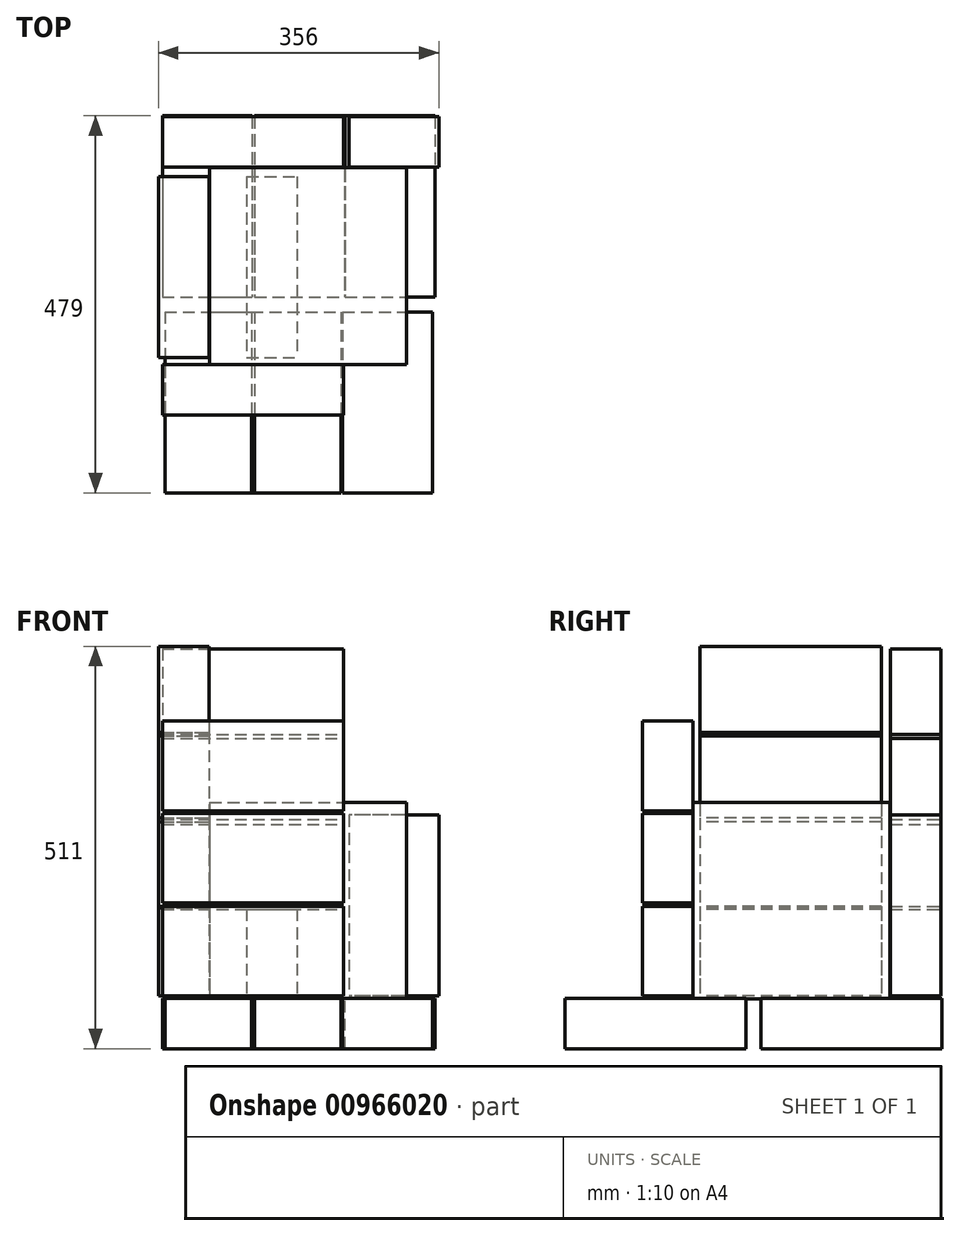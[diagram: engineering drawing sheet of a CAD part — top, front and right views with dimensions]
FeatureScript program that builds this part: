
annotation { "Feature Type Name" : "Feature", "Feature Type Description" : "" }
export const myFeature = defineFeature(function(context is Context, id is Id, definition is map)
    precondition{}
    {
        {
            var Q0;
            Q0=qCreatedBy(makeId("Front.planeOp"),FACE);
            var sketch = newSketch(context, id + "F0", { "sketchPlane" : qUnion([Q0])});
            skLineSegment(sketch, "E0.bottom", {"start": v(0, 114) * mm, "end": v(230, 114) * mm});
            skLineSegment(sketch, "E0.top", {"start": v(0, 0) * mm, "end": v(230, 0) * mm});
            skLineSegment(sketch, "E0.left", {"start": v(0, 114) * mm, "end": v(0, 0) * mm});
            skLineSegment(sketch, "E0.right", {"start": v(230, 114) * mm, "end": v(230, 0) * mm});
            skSolve(sketch);
        }
        {
            var Q0;
            Q0 = qSketchRegion(id + "F0", true);
            extrude(context, id + "F1", {"entities" : qUnion([Q0]), "depth" : 64 * mm, "offsetDistance" : 25 * mm});
        }
        {
            var Q0;
            Q0=qCreatedBy(makeId("Top.planeOp"),FACE);
            var sketch = newSketch(context, id + "F2", { "sketchPlane" : qUnion([Q0])});
            skLineSegment(sketch, "E1.bottom", {"start": v(0, 0) * mm, "end": v(250, 0) * mm});
            skLineSegment(sketch, "E1.top", {"start": v(0, 250) * mm, "end": v(250, 250) * mm});
            skLineSegment(sketch, "E1.left", {"start": v(0, 0) * mm, "end": v(0, 250) * mm});
            skLineSegment(sketch, "E1.right", {"start": v(250, 0) * mm, "end": v(250, 250) * mm});
            skSolve(sketch);
        }
        {
            var Q0;
            Q0 = qSketchRegion(id + "F2", true);
            extrude(context, id + "F3", {"entities" : qUnion([Q0]), "depth" : 250 * mm, "offsetDistance" : 25 * mm});
        }
        {
            var Q0;
            Q0=makeQuery(id+"F1.opExtrude","SWEPT_BODY",BODY,{"disambiguationData":[OSD([sQuery(id+"F0.wireOp",EDGE,"E0.bottom"),sQuery(id+"F0.wireOp",EDGE,"E0.top"),sQuery(id+"F0.wireOp",EDGE,"E0.left"),sQuery(id+"F0.wireOp",EDGE,"E0.right")])]});
            transform(context, id + "F4", {"entities" : qUnion([Q0]), "transformType" : TransformType.TRANSLATION_3D, "dx" : -60 * mm, "dy" : 0 * mm, "dz" : 110 * mm, "makeCopy" : true});
        }
        {
            var Q0;
            Q0=makeQuery(id+"F1.opExtrude","SWEPT_BODY",BODY,{"disambiguationData":[OSD([sQuery(id+"F0.wireOp",EDGE,"E0.bottom"),sQuery(id+"F0.wireOp",EDGE,"E0.top"),sQuery(id+"F0.wireOp",EDGE,"E0.left"),sQuery(id+"F0.wireOp",EDGE,"E0.right")])]});
            transform(context, id + "F5", {"entities" : qUnion([Q0]), "transformType" : TransformType.TRANSLATION_3D, "dx" : -60 * mm, "dy" : 0 * mm, "dz" : 0 * mm, "makeCopy" : false});
        }
        {
            var Q0;
            Q0=makeQuery(id+"F4.opPattern","COPY",BODY,{"derivedFrom":makeQuery(id+"F1.opExtrude","SWEPT_BODY",BODY,{"disambiguationData":[OSD([sQuery(id+"F0.wireOp",EDGE,"E0.bottom"),sQuery(id+"F0.wireOp",EDGE,"E0.top"),sQuery(id+"F0.wireOp",EDGE,"E0.left"),sQuery(id+"F0.wireOp",EDGE,"E0.right")])]}),"instanceName":"1"});
            transform(context, id + "F6", {"entities" : qUnion([Q0]), "transformType" : TransformType.TRANSLATION_3D, "dx" : 0 * mm, "dy" : 315 * mm, "dz" : 0 * mm, "makeCopy" : true});
        }
        {
            var Q0;
            Q0=makeQuery(id+"F1.opExtrude","SWEPT_BODY",BODY,{"disambiguationData":[OSD([sQuery(id+"F0.wireOp",EDGE,"E0.bottom"),sQuery(id+"F0.wireOp",EDGE,"E0.top"),sQuery(id+"F0.wireOp",EDGE,"E0.left"),sQuery(id+"F0.wireOp",EDGE,"E0.right")])]});
            transform(context, id + "F7", {"entities" : qUnion([Q0]), "transformType" : TransformType.TRANSLATION_3D, "dx" : 0 * mm, "dy" : 315 * mm, "dz" : 0 * mm, "makeCopy" : true});
        }
        {
            var Q0;
            Q0=makeQuery(id+"F1.opExtrude","SWEPT_BODY",BODY,{"disambiguationData":[OSD([sQuery(id+"F0.wireOp",EDGE,"E0.bottom"),sQuery(id+"F0.wireOp",EDGE,"E0.top"),sQuery(id+"F0.wireOp",EDGE,"E0.left"),sQuery(id+"F0.wireOp",EDGE,"E0.right")])]});
            transform(context, id + "F8", {"entities" : qUnion([Q0]), "transformType" : TransformType.TRANSLATION_3D, "dx" : -284 * mm, "dy" : 0 * mm, "dz" : 0 * mm, "makeCopy" : true});
        }
        {
            var Q0;
            Q0=makeQuery(id+"F8.opPattern","COPY",BODY,{"derivedFrom":makeQuery(id+"F1.opExtrude","SWEPT_BODY",BODY,{"disambiguationData":[OSD([sQuery(id+"F0.wireOp",EDGE,"E0.bottom"),sQuery(id+"F0.wireOp",EDGE,"E0.top"),sQuery(id+"F0.wireOp",EDGE,"E0.left"),sQuery(id+"F0.wireOp",EDGE,"E0.right")])]}),"instanceName":"1"});
            var Q1;
            Q1=makeQuery(id+"F8.opPattern","COPY",EDGE,{"derivedFrom":makeQuery(id+"F1.opExtrude","CAP_EDGE",EDGE,{"disambiguationData":[OSD([sQuery(id+"F0.wireOp",EDGE,"E0.left")])],"isStart":true}),"instanceName":"1"});
            transform(context, id + "F9", {"entities" : qUnion([Q0]), "transformType" : TransformType.ROTATION, "transformAxis" : qUnion([Q1]), "angle" : 90 * degree, "makeCopy" : false});
        }
        {
            var Q0;
            Q0=makeQuery(id+"F8.opPattern","COPY",BODY,{"derivedFrom":makeQuery(id+"F1.opExtrude","SWEPT_BODY",BODY,{"disambiguationData":[OSD([sQuery(id+"F0.wireOp",EDGE,"E0.bottom"),sQuery(id+"F0.wireOp",EDGE,"E0.top"),sQuery(id+"F0.wireOp",EDGE,"E0.left"),sQuery(id+"F0.wireOp",EDGE,"E0.right")])]}),"instanceName":"1"});
            transform(context, id + "F10", {"entities" : qUnion([Q0]), "transformType" : TransformType.TRANSLATION_3D, "dx" : 343 * mm, "dy" : 239 * mm, "dz" : 0 * mm, "makeCopy" : false});
        }
        {
            var Q0;
            Q0=makeQuery(id+"F1.opExtrude","SWEPT_BODY",BODY,{"disambiguationData":[OSD([sQuery(id+"F0.wireOp",EDGE,"E0.bottom"),sQuery(id+"F0.wireOp",EDGE,"E0.top"),sQuery(id+"F0.wireOp",EDGE,"E0.left"),sQuery(id+"F0.wireOp",EDGE,"E0.right")])]});
            transform(context, id + "F11", {"entities" : qUnion([Q0]), "transformType" : TransformType.TRANSLATION_3D, "dx" : 0 * mm, "dy" : 0 * mm, "dz" : -113 * mm, "makeCopy" : true});
        }
        {
            var Q0;
            Q0=makeQuery(id+"F11.opPattern","COPY",BODY,{"derivedFrom":makeQuery(id+"F1.opExtrude","SWEPT_BODY",BODY,{"disambiguationData":[OSD([sQuery(id+"F0.wireOp",EDGE,"E0.bottom"),sQuery(id+"F0.wireOp",EDGE,"E0.top"),sQuery(id+"F0.wireOp",EDGE,"E0.left"),sQuery(id+"F0.wireOp",EDGE,"E0.right")])]}),"instanceName":"1"});
            var Q1;
            Q1=makeQuery(id+"F11.opPattern","COPY",EDGE,{"derivedFrom":makeQuery(id+"F1.opExtrude","CAP_EDGE",EDGE,{"disambiguationData":[OSD([sQuery(id+"F0.wireOp",EDGE,"E0.bottom")])],"isStart":true}),"instanceName":"1"});
            transform(context, id + "F12", {"entities" : qUnion([Q0]), "transformType" : TransformType.ROTATION, "transformAxis" : qUnion([Q1]), "angle" : 90 * degree, "makeCopy" : false});
        }
        {
            var Q0;
            Q0=makeQuery(id+"F11.opPattern","COPY",BODY,{"derivedFrom":makeQuery(id+"F1.opExtrude","SWEPT_BODY",BODY,{"disambiguationData":[OSD([sQuery(id+"F0.wireOp",EDGE,"E0.bottom"),sQuery(id+"F0.wireOp",EDGE,"E0.top"),sQuery(id+"F0.wireOp",EDGE,"E0.left"),sQuery(id+"F0.wireOp",EDGE,"E0.right")])]}),"instanceName":"1"});
            transform(context, id + "F13", {"entities" : qUnion([Q0]), "transformType" : TransformType.TRANSLATION_3D, "dx" : 0 * mm, "dy" : 212 * mm, "dz" : 0 * mm, "makeCopy" : true});
        }
        {
            var Q0;
            Q0=makeQuery(id+"F11.opPattern","COPY",BODY,{"derivedFrom":makeQuery(id+"F1.opExtrude","SWEPT_BODY",BODY,{"disambiguationData":[OSD([sQuery(id+"F0.wireOp",EDGE,"E0.bottom"),sQuery(id+"F0.wireOp",EDGE,"E0.top"),sQuery(id+"F0.wireOp",EDGE,"E0.left"),sQuery(id+"F0.wireOp",EDGE,"E0.right")])]}),"instanceName":"1"});
            transform(context, id + "F14", {"entities" : qUnion([Q0]), "transformType" : TransformType.TRANSLATION_3D, "dx" : 0 * mm, "dy" : -5 * mm, "dz" : 0 * mm, "makeCopy" : false});
        }
        {
            var Q0;
            Q0=makeQuery(id+"F13.opPattern","COPY",BODY,{"derivedFrom":makeQuery(id+"F11.opPattern","COPY",BODY,{"derivedFrom":makeQuery(id+"F1.opExtrude","SWEPT_BODY",BODY,{"disambiguationData":[OSD([sQuery(id+"F0.wireOp",EDGE,"E0.bottom"),sQuery(id+"F0.wireOp",EDGE,"E0.top"),sQuery(id+"F0.wireOp",EDGE,"E0.left"),sQuery(id+"F0.wireOp",EDGE,"E0.right")])]}),"instanceName":"1"}),"instanceName":"1"});
            transform(context, id + "F15", {"entities" : qUnion([Q0]), "transformType" : TransformType.TRANSLATION_3D, "dx" : 0 * mm, "dy" : 131 * mm, "dz" : 0 * mm, "makeCopy" : true});
        }
        {
            var Q0;
            Q0=makeQuery(id+"F15.opPattern","COPY",BODY,{"derivedFrom":makeQuery(id+"F13.opPattern","COPY",BODY,{"derivedFrom":makeQuery(id+"F11.opPattern","COPY",BODY,{"derivedFrom":makeQuery(id+"F1.opExtrude","SWEPT_BODY",BODY,{"disambiguationData":[OSD([sQuery(id+"F0.wireOp",EDGE,"E0.bottom"),sQuery(id+"F0.wireOp",EDGE,"E0.top"),sQuery(id+"F0.wireOp",EDGE,"E0.left"),sQuery(id+"F0.wireOp",EDGE,"E0.right")])]}),"instanceName":"1"}),"instanceName":"1"}),"instanceName":"1"});
            var Q1;
            Q1=makeQuery(id+"F15.opPattern","COPY",EDGE,{"derivedFrom":makeQuery(id+"F13.opPattern","COPY",EDGE,{"derivedFrom":makeQuery(id+"F11.opPattern","COPY",EDGE,{"derivedFrom":makeQuery(id+"F1.opExtrude","SWEPT_EDGE",EDGE,{"disambiguationData":[OSD([sQuery(id+"F0.wireOp",EDGE,"E0.bottom"),sQuery(id+"F0.wireOp",EDGE,"E0.left")])]}),"instanceName":"1"}),"instanceName":"1"}),"instanceName":"1"});
            transform(context, id + "F16", {"entities" : qUnion([Q0]), "transformType" : TransformType.ROTATION, "transformAxis" : qUnion([Q1]), "angle" : 90 * degree, "oppositeDirection" : true, "makeCopy" : false});
        }
        {
            var Q0;
            Q0=makeQuery(id+"F15.opPattern","COPY",BODY,{"derivedFrom":makeQuery(id+"F13.opPattern","COPY",BODY,{"derivedFrom":makeQuery(id+"F11.opPattern","COPY",BODY,{"derivedFrom":makeQuery(id+"F1.opExtrude","SWEPT_BODY",BODY,{"disambiguationData":[OSD([sQuery(id+"F0.wireOp",EDGE,"E0.bottom"),sQuery(id+"F0.wireOp",EDGE,"E0.top"),sQuery(id+"F0.wireOp",EDGE,"E0.left"),sQuery(id+"F0.wireOp",EDGE,"E0.right")])]}),"instanceName":"1"}),"instanceName":"1"}),"instanceName":"1"});
            transform(context, id + "F17", {"entities" : qUnion([Q0]), "transformType" : TransformType.TRANSLATION_3D, "dx" : 0 * mm, "dy" : -27 * mm, "dz" : 0 * mm, "makeCopy" : false});
        }
        {
            var Q0;
            Q0=makeQuery(id+"F13.opPattern","COPY",BODY,{"derivedFrom":makeQuery(id+"F11.opPattern","COPY",BODY,{"derivedFrom":makeQuery(id+"F1.opExtrude","SWEPT_BODY",BODY,{"disambiguationData":[OSD([sQuery(id+"F0.wireOp",EDGE,"E0.bottom"),sQuery(id+"F0.wireOp",EDGE,"E0.top"),sQuery(id+"F0.wireOp",EDGE,"E0.left"),sQuery(id+"F0.wireOp",EDGE,"E0.right")])]}),"instanceName":"1"}),"instanceName":"1"});
            deleteBodies(context, id + "F18", {"entities" : qUnion([Q0])});
        }
        {
            var Q0;
            Q0=makeQuery(id+"F11.opPattern","COPY",BODY,{"derivedFrom":makeQuery(id+"F1.opExtrude","SWEPT_BODY",BODY,{"disambiguationData":[OSD([sQuery(id+"F0.wireOp",EDGE,"E0.bottom"),sQuery(id+"F0.wireOp",EDGE,"E0.top"),sQuery(id+"F0.wireOp",EDGE,"E0.left"),sQuery(id+"F0.wireOp",EDGE,"E0.right")])]}),"instanceName":"1"});
            deleteBodies(context, id + "F19", {"entities" : qUnion([Q0])});
        }
        {
            var Q0;
            Q0=makeQuery(id+"F15.opPattern","COPY",BODY,{"derivedFrom":makeQuery(id+"F13.opPattern","COPY",BODY,{"derivedFrom":makeQuery(id+"F11.opPattern","COPY",BODY,{"derivedFrom":makeQuery(id+"F1.opExtrude","SWEPT_BODY",BODY,{"disambiguationData":[OSD([sQuery(id+"F0.wireOp",EDGE,"E0.bottom"),sQuery(id+"F0.wireOp",EDGE,"E0.top"),sQuery(id+"F0.wireOp",EDGE,"E0.left"),sQuery(id+"F0.wireOp",EDGE,"E0.right")])]}),"instanceName":"1"}),"instanceName":"1"}),"instanceName":"1"});
            transform(context, id + "F20", {"entities" : qUnion([Q0]), "transformType" : TransformType.TRANSLATION_3D, "dx" : 0 * mm, "dy" : -236 * mm, "dz" : 0 * mm, "makeCopy" : true});
        }
        {
            var Q0;
            Q0=makeQuery(id+"F20.opPattern","COPY",BODY,{"derivedFrom":makeQuery(id+"F15.opPattern","COPY",BODY,{"derivedFrom":makeQuery(id+"F13.opPattern","COPY",BODY,{"derivedFrom":makeQuery(id+"F11.opPattern","COPY",BODY,{"derivedFrom":makeQuery(id+"F1.opExtrude","SWEPT_BODY",BODY,{"disambiguationData":[OSD([sQuery(id+"F0.wireOp",EDGE,"E0.bottom"),sQuery(id+"F0.wireOp",EDGE,"E0.top"),sQuery(id+"F0.wireOp",EDGE,"E0.left"),sQuery(id+"F0.wireOp",EDGE,"E0.right")])]}),"instanceName":"1"}),"instanceName":"1"}),"instanceName":"1"}),"instanceName":"1"});
            var Q1;
            Q1=makeQuery(id+"F20.opPattern","COPY",EDGE,{"derivedFrom":makeQuery(id+"F15.opPattern","COPY",EDGE,{"derivedFrom":makeQuery(id+"F13.opPattern","COPY",EDGE,{"derivedFrom":makeQuery(id+"F11.opPattern","COPY",EDGE,{"derivedFrom":makeQuery(id+"F1.opExtrude","SWEPT_EDGE",EDGE,{"disambiguationData":[OSD([sQuery(id+"F0.wireOp",EDGE,"E0.top"),sQuery(id+"F0.wireOp",EDGE,"E0.left")])]}),"instanceName":"1"}),"instanceName":"1"}),"instanceName":"1"}),"instanceName":"1"});
            transform(context, id + "F21", {"entities" : qUnion([Q0]), "transformType" : TransformType.ROTATION, "transformAxis" : qUnion([Q1]), "angle" : 90 * degree, "makeCopy" : false});
        }
        {
            var Q0;
            Q0=makeQuery(id+"F15.opPattern","COPY",BODY,{"derivedFrom":makeQuery(id+"F13.opPattern","COPY",BODY,{"derivedFrom":makeQuery(id+"F11.opPattern","COPY",BODY,{"derivedFrom":makeQuery(id+"F1.opExtrude","SWEPT_BODY",BODY,{"disambiguationData":[OSD([sQuery(id+"F0.wireOp",EDGE,"E0.bottom"),sQuery(id+"F0.wireOp",EDGE,"E0.top"),sQuery(id+"F0.wireOp",EDGE,"E0.left"),sQuery(id+"F0.wireOp",EDGE,"E0.right")])]}),"instanceName":"1"}),"instanceName":"1"}),"instanceName":"1"});
            transform(context, id + "F22", {"entities" : qUnion([Q0]), "transformType" : TransformType.TRANSLATION_3D, "dx" : 108 * mm, "dy" : 0 * mm, "dz" : 0 * mm, "makeCopy" : true});
        }
        {
            var Q0;
            Q0=makeQuery(id+"F20.opPattern","COPY",BODY,{"derivedFrom":makeQuery(id+"F15.opPattern","COPY",BODY,{"derivedFrom":makeQuery(id+"F13.opPattern","COPY",BODY,{"derivedFrom":makeQuery(id+"F11.opPattern","COPY",BODY,{"derivedFrom":makeQuery(id+"F1.opExtrude","SWEPT_BODY",BODY,{"disambiguationData":[OSD([sQuery(id+"F0.wireOp",EDGE,"E0.bottom"),sQuery(id+"F0.wireOp",EDGE,"E0.top"),sQuery(id+"F0.wireOp",EDGE,"E0.left"),sQuery(id+"F0.wireOp",EDGE,"E0.right")])]}),"instanceName":"1"}),"instanceName":"1"}),"instanceName":"1"}),"instanceName":"1"});
            var Q1;
            Q1=makeQuery(id+"F20.opPattern","COPY",EDGE,{"derivedFrom":makeQuery(id+"F15.opPattern","COPY",EDGE,{"derivedFrom":makeQuery(id+"F13.opPattern","COPY",EDGE,{"derivedFrom":makeQuery(id+"F11.opPattern","COPY",EDGE,{"derivedFrom":makeQuery(id+"F1.opExtrude","SWEPT_EDGE",EDGE,{"disambiguationData":[OSD([sQuery(id+"F0.wireOp",EDGE,"E0.bottom"),sQuery(id+"F0.wireOp",EDGE,"E0.left")])]}),"instanceName":"1"}),"instanceName":"1"}),"instanceName":"1"}),"instanceName":"1"});
            transform(context, id + "F23", {"entities" : qUnion([Q0]), "transformType" : TransformType.ROTATION, "transformAxis" : qUnion([Q1]), "angle" : 90 * degree, "oppositeDirection" : true, "makeCopy" : true});
        }
        {
            var Q0;
            Q0=makeQuery(id+"F23.opPattern","COPY",BODY,{"derivedFrom":makeQuery(id+"F20.opPattern","COPY",BODY,{"derivedFrom":makeQuery(id+"F15.opPattern","COPY",BODY,{"derivedFrom":makeQuery(id+"F13.opPattern","COPY",BODY,{"derivedFrom":makeQuery(id+"F11.opPattern","COPY",BODY,{"derivedFrom":makeQuery(id+"F1.opExtrude","SWEPT_BODY",BODY,{"disambiguationData":[OSD([sQuery(id+"F0.wireOp",EDGE,"E0.bottom"),sQuery(id+"F0.wireOp",EDGE,"E0.top"),sQuery(id+"F0.wireOp",EDGE,"E0.left"),sQuery(id+"F0.wireOp",EDGE,"E0.right")])]}),"instanceName":"1"}),"instanceName":"1"}),"instanceName":"1"}),"instanceName":"1"}),"instanceName":"1"});
            transform(context, id + "F24", {"entities" : qUnion([Q0]), "transformType" : TransformType.TRANSLATION_3D, "dx" : -111 * mm, "dy" : 101 * mm, "dz" : 0 * mm, "makeCopy" : false});
        }
        {
            var Q0;
            Q0=makeQuery(id+"F20.opPattern","COPY",BODY,{"derivedFrom":makeQuery(id+"F15.opPattern","COPY",BODY,{"derivedFrom":makeQuery(id+"F13.opPattern","COPY",BODY,{"derivedFrom":makeQuery(id+"F11.opPattern","COPY",BODY,{"derivedFrom":makeQuery(id+"F1.opExtrude","SWEPT_BODY",BODY,{"disambiguationData":[OSD([sQuery(id+"F0.wireOp",EDGE,"E0.bottom"),sQuery(id+"F0.wireOp",EDGE,"E0.top"),sQuery(id+"F0.wireOp",EDGE,"E0.left"),sQuery(id+"F0.wireOp",EDGE,"E0.right")])]}),"instanceName":"1"}),"instanceName":"1"}),"instanceName":"1"}),"instanceName":"1"});
            deleteBodies(context, id + "F25", {"entities" : qUnion([Q0])});
        }
        {
            var Q0;
            Q0=makeQuery(id+"F23.opPattern","COPY",BODY,{"derivedFrom":makeQuery(id+"F20.opPattern","COPY",BODY,{"derivedFrom":makeQuery(id+"F15.opPattern","COPY",BODY,{"derivedFrom":makeQuery(id+"F13.opPattern","COPY",BODY,{"derivedFrom":makeQuery(id+"F11.opPattern","COPY",BODY,{"derivedFrom":makeQuery(id+"F1.opExtrude","SWEPT_BODY",BODY,{"disambiguationData":[OSD([sQuery(id+"F0.wireOp",EDGE,"E0.bottom"),sQuery(id+"F0.wireOp",EDGE,"E0.top"),sQuery(id+"F0.wireOp",EDGE,"E0.left"),sQuery(id+"F0.wireOp",EDGE,"E0.right")])]}),"instanceName":"1"}),"instanceName":"1"}),"instanceName":"1"}),"instanceName":"1"}),"instanceName":"1"});
            transform(context, id + "F26", {"entities" : qUnion([Q0]), "transformType" : TransformType.TRANSLATION_3D, "dx" : 110 * mm, "dy" : 0 * mm, "dz" : 0 * mm, "makeCopy" : true});
        }
        {
            var Q0;
            Q0=makeQuery(id+"F22.opPattern","COPY",BODY,{"derivedFrom":makeQuery(id+"F15.opPattern","COPY",BODY,{"derivedFrom":makeQuery(id+"F13.opPattern","COPY",BODY,{"derivedFrom":makeQuery(id+"F11.opPattern","COPY",BODY,{"derivedFrom":makeQuery(id+"F1.opExtrude","SWEPT_BODY",BODY,{"disambiguationData":[OSD([sQuery(id+"F0.wireOp",EDGE,"E0.bottom"),sQuery(id+"F0.wireOp",EDGE,"E0.top"),sQuery(id+"F0.wireOp",EDGE,"E0.left"),sQuery(id+"F0.wireOp",EDGE,"E0.right")])]}),"instanceName":"1"}),"instanceName":"1"}),"instanceName":"1"}),"instanceName":"1"});
            transform(context, id + "F27", {"entities" : qUnion([Q0]), "transformType" : TransformType.TRANSLATION_3D, "dx" : 112 * mm, "dy" : 0 * mm, "dz" : 0 * mm, "makeCopy" : true});
        }
        {
            var Q0;
            Q0=makeQuery(id+"F8.opPattern","COPY",BODY,{"derivedFrom":makeQuery(id+"F1.opExtrude","SWEPT_BODY",BODY,{"disambiguationData":[OSD([sQuery(id+"F0.wireOp",EDGE,"E0.bottom"),sQuery(id+"F0.wireOp",EDGE,"E0.top"),sQuery(id+"F0.wireOp",EDGE,"E0.left"),sQuery(id+"F0.wireOp",EDGE,"E0.right")])]}),"instanceName":"1"});
            transform(context, id + "F28", {"entities" : qUnion([Q0]), "transformType" : TransformType.TRANSLATION_3D, "dx" : 112 * mm, "dy" : 0 * mm, "dz" : 0 * mm, "makeCopy" : true});
        }
        {
            var Q0;
            Q0=makeQuery(id+"F8.opPattern","COPY",BODY,{"derivedFrom":makeQuery(id+"F1.opExtrude","SWEPT_BODY",BODY,{"disambiguationData":[OSD([sQuery(id+"F0.wireOp",EDGE,"E0.bottom"),sQuery(id+"F0.wireOp",EDGE,"E0.top"),sQuery(id+"F0.wireOp",EDGE,"E0.left"),sQuery(id+"F0.wireOp",EDGE,"E0.right")])]}),"instanceName":"1"});
            transform(context, id + "F29", {"entities" : qUnion([Q0]), "transformType" : TransformType.TRANSLATION_3D, "dx" : 0 * mm, "dy" : 0 * mm, "dz" : 112 * mm, "makeCopy" : true});
        }
        {
            var Q0;
            Q0=makeQuery(id+"F6.opPattern","COPY",BODY,{"derivedFrom":makeQuery(id+"F4.opPattern","COPY",BODY,{"derivedFrom":makeQuery(id+"F1.opExtrude","SWEPT_BODY",BODY,{"disambiguationData":[OSD([sQuery(id+"F0.wireOp",EDGE,"E0.bottom"),sQuery(id+"F0.wireOp",EDGE,"E0.top"),sQuery(id+"F0.wireOp",EDGE,"E0.left"),sQuery(id+"F0.wireOp",EDGE,"E0.right")])]}),"instanceName":"1"}),"instanceName":"1"});
            transform(context, id + "F30", {"entities" : qUnion([Q0]), "transformType" : TransformType.TRANSLATION_3D, "dx" : 0 * mm, "dy" : 0 * mm, "dz" : 108 * mm, "makeCopy" : true});
        }
        {
            var Q0;
            Q0=makeQuery(id+"F7.opPattern","COPY",BODY,{"derivedFrom":makeQuery(id+"F1.opExtrude","SWEPT_BODY",BODY,{"disambiguationData":[OSD([sQuery(id+"F0.wireOp",EDGE,"E0.bottom"),sQuery(id+"F0.wireOp",EDGE,"E0.top"),sQuery(id+"F0.wireOp",EDGE,"E0.left"),sQuery(id+"F0.wireOp",EDGE,"E0.right")])]}),"instanceName":"1"});
            transform(context, id + "F31", {"entities" : qUnion([Q0]), "transformType" : TransformType.TRANSLATION_3D, "dx" : 7 * mm, "dy" : 0 * mm, "dz" : 0 * mm, "makeCopy" : true});
        }
        {
            var Q0;
            Q0=makeQuery(id+"F31.opPattern","COPY",BODY,{"derivedFrom":makeQuery(id+"F7.opPattern","COPY",BODY,{"derivedFrom":makeQuery(id+"F1.opExtrude","SWEPT_BODY",BODY,{"disambiguationData":[OSD([sQuery(id+"F0.wireOp",EDGE,"E0.bottom"),sQuery(id+"F0.wireOp",EDGE,"E0.top"),sQuery(id+"F0.wireOp",EDGE,"E0.left"),sQuery(id+"F0.wireOp",EDGE,"E0.right")])]}),"instanceName":"1"}),"instanceName":"1"});
            var Q1;
            Q1=makeQuery(id+"F31.opPattern","COPY",EDGE,{"derivedFrom":makeQuery(id+"F7.opPattern","COPY",EDGE,{"derivedFrom":makeQuery(id+"F1.opExtrude","SWEPT_EDGE",EDGE,{"disambiguationData":[OSD([sQuery(id+"F0.wireOp",EDGE,"E0.top"),sQuery(id+"F0.wireOp",EDGE,"E0.right")])]}),"instanceName":"1"}),"instanceName":"1"});
            transform(context, id + "F32", {"entities" : qUnion([Q0]), "transformType" : TransformType.ROTATION, "transformAxis" : qUnion([Q1]), "angle" : 90 * degree, "makeCopy" : false});
        }
        {
            var Q0;
            Q0=makeQuery(id+"F30.opPattern","COPY",BODY,{"derivedFrom":makeQuery(id+"F6.opPattern","COPY",BODY,{"derivedFrom":makeQuery(id+"F4.opPattern","COPY",BODY,{"derivedFrom":makeQuery(id+"F1.opExtrude","SWEPT_BODY",BODY,{"disambiguationData":[OSD([sQuery(id+"F0.wireOp",EDGE,"E0.bottom"),sQuery(id+"F0.wireOp",EDGE,"E0.top"),sQuery(id+"F0.wireOp",EDGE,"E0.left"),sQuery(id+"F0.wireOp",EDGE,"E0.right")])]}),"instanceName":"1"}),"instanceName":"1"}),"instanceName":"1"});
            var Q1;
            Q1=makeQuery(id+"F29.opPattern","COPY",BODY,{"derivedFrom":makeQuery(id+"F8.opPattern","COPY",BODY,{"derivedFrom":makeQuery(id+"F1.opExtrude","SWEPT_BODY",BODY,{"disambiguationData":[OSD([sQuery(id+"F0.wireOp",EDGE,"E0.bottom"),sQuery(id+"F0.wireOp",EDGE,"E0.top"),sQuery(id+"F0.wireOp",EDGE,"E0.left"),sQuery(id+"F0.wireOp",EDGE,"E0.right")])]}),"instanceName":"1"}),"instanceName":"1"});
            transform(context, id + "F33", {"entities" : qUnion([Q0, Q1]), "transformType" : TransformType.TRANSLATION_3D, "dx" : 0 * mm, "dy" : 0 * mm, "dz" : 109 * mm, "makeCopy" : true});
        }
        {
            var Q0;
            Q0=makeQuery(id+"F33.opPattern","COPY",BODY,{"derivedFrom":makeQuery(id+"F29.opPattern","COPY",BODY,{"derivedFrom":makeQuery(id+"F8.opPattern","COPY",BODY,{"derivedFrom":makeQuery(id+"F1.opExtrude","SWEPT_BODY",BODY,{"disambiguationData":[OSD([sQuery(id+"F0.wireOp",EDGE,"E0.bottom"),sQuery(id+"F0.wireOp",EDGE,"E0.top"),sQuery(id+"F0.wireOp",EDGE,"E0.left"),sQuery(id+"F0.wireOp",EDGE,"E0.right")])]}),"instanceName":"1"}),"instanceName":"1"}),"instanceName":"1"});
            transform(context, id + "F34", {"entities" : qUnion([Q0]), "transformType" : TransformType.TRANSLATION_3D, "dx" : 0 * mm, "dy" : 0 * mm, "dz" : 109 * mm, "makeCopy" : true});
        }
        {
            var Q0;
            Q0=makeQuery(id+"F27.opPattern","COPY",BODY,{"derivedFrom":makeQuery(id+"F22.opPattern","COPY",BODY,{"derivedFrom":makeQuery(id+"F15.opPattern","COPY",BODY,{"derivedFrom":makeQuery(id+"F13.opPattern","COPY",BODY,{"derivedFrom":makeQuery(id+"F11.opPattern","COPY",BODY,{"derivedFrom":makeQuery(id+"F1.opExtrude","SWEPT_BODY",BODY,{"disambiguationData":[OSD([sQuery(id+"F0.wireOp",EDGE,"E0.bottom"),sQuery(id+"F0.wireOp",EDGE,"E0.top"),sQuery(id+"F0.wireOp",EDGE,"E0.left"),sQuery(id+"F0.wireOp",EDGE,"E0.right")])]}),"instanceName":"1"}),"instanceName":"1"}),"instanceName":"1"}),"instanceName":"1"}),"instanceName":"1"});
            transform(context, id + "F35", {"entities" : qUnion([Q0]), "transformType" : TransformType.TRANSLATION_3D, "dx" : 112 * mm, "dy" : 0 * mm, "dz" : 0 * mm, "makeCopy" : true});
        }
        {
            var Q0;
            Q0=makeQuery(id+"F4.opPattern","COPY",BODY,{"derivedFrom":makeQuery(id+"F1.opExtrude","SWEPT_BODY",BODY,{"disambiguationData":[OSD([sQuery(id+"F0.wireOp",EDGE,"E0.bottom"),sQuery(id+"F0.wireOp",EDGE,"E0.top"),sQuery(id+"F0.wireOp",EDGE,"E0.left"),sQuery(id+"F0.wireOp",EDGE,"E0.right")])]}),"instanceName":"1"});
            transform(context, id + "F36", {"entities" : qUnion([Q0]), "transformType" : TransformType.TRANSLATION_3D, "dx" : 0 * mm, "dy" : 0 * mm, "dz" : 8 * mm, "makeCopy" : false});
        }
        {
            var Q0;
            Q0=makeQuery(id+"F35.opPattern","COPY",BODY,{"derivedFrom":makeQuery(id+"F27.opPattern","COPY",BODY,{"derivedFrom":makeQuery(id+"F22.opPattern","COPY",BODY,{"derivedFrom":makeQuery(id+"F15.opPattern","COPY",BODY,{"derivedFrom":makeQuery(id+"F13.opPattern","COPY",BODY,{"derivedFrom":makeQuery(id+"F11.opPattern","COPY",BODY,{"derivedFrom":makeQuery(id+"F1.opExtrude","SWEPT_BODY",BODY,{"disambiguationData":[OSD([sQuery(id+"F0.wireOp",EDGE,"E0.bottom"),sQuery(id+"F0.wireOp",EDGE,"E0.top"),sQuery(id+"F0.wireOp",EDGE,"E0.left"),sQuery(id+"F0.wireOp",EDGE,"E0.right")])]}),"instanceName":"1"}),"instanceName":"1"}),"instanceName":"1"}),"instanceName":"1"}),"instanceName":"1"}),"instanceName":"1"});
            deleteBodies(context, id + "F37", {"entities" : qUnion([Q0])});
        }
        {
            var Q0;
            Q0=makeQuery(id+"F22.opPattern","COPY",BODY,{"derivedFrom":makeQuery(id+"F15.opPattern","COPY",BODY,{"derivedFrom":makeQuery(id+"F13.opPattern","COPY",BODY,{"derivedFrom":makeQuery(id+"F11.opPattern","COPY",BODY,{"derivedFrom":makeQuery(id+"F1.opExtrude","SWEPT_BODY",BODY,{"disambiguationData":[OSD([sQuery(id+"F0.wireOp",EDGE,"E0.bottom"),sQuery(id+"F0.wireOp",EDGE,"E0.top"),sQuery(id+"F0.wireOp",EDGE,"E0.left"),sQuery(id+"F0.wireOp",EDGE,"E0.right")])]}),"instanceName":"1"}),"instanceName":"1"}),"instanceName":"1"}),"instanceName":"1"});
            var Q1;
            Q1=makeQuery(id+"F27.opPattern","COPY",BODY,{"derivedFrom":makeQuery(id+"F22.opPattern","COPY",BODY,{"derivedFrom":makeQuery(id+"F15.opPattern","COPY",BODY,{"derivedFrom":makeQuery(id+"F13.opPattern","COPY",BODY,{"derivedFrom":makeQuery(id+"F11.opPattern","COPY",BODY,{"derivedFrom":makeQuery(id+"F1.opExtrude","SWEPT_BODY",BODY,{"disambiguationData":[OSD([sQuery(id+"F0.wireOp",EDGE,"E0.bottom"),sQuery(id+"F0.wireOp",EDGE,"E0.top"),sQuery(id+"F0.wireOp",EDGE,"E0.left"),sQuery(id+"F0.wireOp",EDGE,"E0.right")])]}),"instanceName":"1"}),"instanceName":"1"}),"instanceName":"1"}),"instanceName":"1"}),"instanceName":"1"});
            transform(context, id + "F38", {"entities" : qUnion([Q0, Q1]), "transformType" : TransformType.TRANSLATION_3D, "dx" : 9 * mm, "dy" : 0 * mm, "dz" : 0 * mm, "makeCopy" : false});
        }
        {
            var Q0;
            Q0=makeQuery(id+"F27.opPattern","COPY",BODY,{"derivedFrom":makeQuery(id+"F22.opPattern","COPY",BODY,{"derivedFrom":makeQuery(id+"F15.opPattern","COPY",BODY,{"derivedFrom":makeQuery(id+"F13.opPattern","COPY",BODY,{"derivedFrom":makeQuery(id+"F11.opPattern","COPY",BODY,{"derivedFrom":makeQuery(id+"F1.opExtrude","SWEPT_BODY",BODY,{"disambiguationData":[OSD([sQuery(id+"F0.wireOp",EDGE,"E0.bottom"),sQuery(id+"F0.wireOp",EDGE,"E0.top"),sQuery(id+"F0.wireOp",EDGE,"E0.left"),sQuery(id+"F0.wireOp",EDGE,"E0.right")])]}),"instanceName":"1"}),"instanceName":"1"}),"instanceName":"1"}),"instanceName":"1"}),"instanceName":"1"});
            transform(context, id + "F39", {"entities" : qUnion([Q0]), "transformType" : TransformType.TRANSLATION_3D, "dx" : 3 * mm, "dy" : 0 * mm, "dz" : 0 * mm, "makeCopy" : false});
        }
        {
            var Q0;
            Q0=makeQuery(id+"F31.opPattern","COPY",BODY,{"derivedFrom":makeQuery(id+"F7.opPattern","COPY",BODY,{"derivedFrom":makeQuery(id+"F1.opExtrude","SWEPT_BODY",BODY,{"disambiguationData":[OSD([sQuery(id+"F0.wireOp",EDGE,"E0.bottom"),sQuery(id+"F0.wireOp",EDGE,"E0.top"),sQuery(id+"F0.wireOp",EDGE,"E0.left"),sQuery(id+"F0.wireOp",EDGE,"E0.right")])]}),"instanceName":"1"}),"instanceName":"1"});
            var Q1;
            Q1=makeQuery(id+"F6.opPattern","COPY",BODY,{"derivedFrom":makeQuery(id+"F4.opPattern","COPY",BODY,{"derivedFrom":makeQuery(id+"F1.opExtrude","SWEPT_BODY",BODY,{"disambiguationData":[OSD([sQuery(id+"F0.wireOp",EDGE,"E0.bottom"),sQuery(id+"F0.wireOp",EDGE,"E0.top"),sQuery(id+"F0.wireOp",EDGE,"E0.left"),sQuery(id+"F0.wireOp",EDGE,"E0.right")])]}),"instanceName":"1"}),"instanceName":"1"});
            var Q2;
            Q2=makeQuery(id+"F30.opPattern","COPY",BODY,{"derivedFrom":makeQuery(id+"F6.opPattern","COPY",BODY,{"derivedFrom":makeQuery(id+"F4.opPattern","COPY",BODY,{"derivedFrom":makeQuery(id+"F1.opExtrude","SWEPT_BODY",BODY,{"disambiguationData":[OSD([sQuery(id+"F0.wireOp",EDGE,"E0.bottom"),sQuery(id+"F0.wireOp",EDGE,"E0.top"),sQuery(id+"F0.wireOp",EDGE,"E0.left"),sQuery(id+"F0.wireOp",EDGE,"E0.right")])]}),"instanceName":"1"}),"instanceName":"1"}),"instanceName":"1"});
            var Q3;
            Q3=makeQuery(id+"F33.opPattern","COPY",BODY,{"derivedFrom":makeQuery(id+"F30.opPattern","COPY",BODY,{"derivedFrom":makeQuery(id+"F6.opPattern","COPY",BODY,{"derivedFrom":makeQuery(id+"F4.opPattern","COPY",BODY,{"derivedFrom":makeQuery(id+"F1.opExtrude","SWEPT_BODY",BODY,{"disambiguationData":[OSD([sQuery(id+"F0.wireOp",EDGE,"E0.bottom"),sQuery(id+"F0.wireOp",EDGE,"E0.top"),sQuery(id+"F0.wireOp",EDGE,"E0.left"),sQuery(id+"F0.wireOp",EDGE,"E0.right")])]}),"instanceName":"1"}),"instanceName":"1"}),"instanceName":"1"}),"instanceName":"1"});
            var Q4;
            Q4=makeQuery(id+"F7.opPattern","COPY",BODY,{"derivedFrom":makeQuery(id+"F1.opExtrude","SWEPT_BODY",BODY,{"disambiguationData":[OSD([sQuery(id+"F0.wireOp",EDGE,"E0.bottom"),sQuery(id+"F0.wireOp",EDGE,"E0.top"),sQuery(id+"F0.wireOp",EDGE,"E0.left"),sQuery(id+"F0.wireOp",EDGE,"E0.right")])]}),"instanceName":"1"});
            var Q5;
            Q5=makeQuery(id+"F8.opPattern","COPY",BODY,{"derivedFrom":makeQuery(id+"F1.opExtrude","SWEPT_BODY",BODY,{"disambiguationData":[OSD([sQuery(id+"F0.wireOp",EDGE,"E0.bottom"),sQuery(id+"F0.wireOp",EDGE,"E0.top"),sQuery(id+"F0.wireOp",EDGE,"E0.left"),sQuery(id+"F0.wireOp",EDGE,"E0.right")])]}),"instanceName":"1"});
            var Q6;
            Q6=makeQuery(id+"F1.opExtrude","SWEPT_BODY",BODY,{"disambiguationData":[OSD([sQuery(id+"F0.wireOp",EDGE,"E0.bottom"),sQuery(id+"F0.wireOp",EDGE,"E0.top"),sQuery(id+"F0.wireOp",EDGE,"E0.left"),sQuery(id+"F0.wireOp",EDGE,"E0.right")])]});
            var Q7;
            Q7=makeQuery(id+"F4.opPattern","COPY",BODY,{"derivedFrom":makeQuery(id+"F1.opExtrude","SWEPT_BODY",BODY,{"disambiguationData":[OSD([sQuery(id+"F0.wireOp",EDGE,"E0.bottom"),sQuery(id+"F0.wireOp",EDGE,"E0.top"),sQuery(id+"F0.wireOp",EDGE,"E0.left"),sQuery(id+"F0.wireOp",EDGE,"E0.right")])]}),"instanceName":"1"});
            var Q8;
            Q8=makeQuery(id+"F29.opPattern","COPY",BODY,{"derivedFrom":makeQuery(id+"F8.opPattern","COPY",BODY,{"derivedFrom":makeQuery(id+"F1.opExtrude","SWEPT_BODY",BODY,{"disambiguationData":[OSD([sQuery(id+"F0.wireOp",EDGE,"E0.bottom"),sQuery(id+"F0.wireOp",EDGE,"E0.top"),sQuery(id+"F0.wireOp",EDGE,"E0.left"),sQuery(id+"F0.wireOp",EDGE,"E0.right")])]}),"instanceName":"1"}),"instanceName":"1"});
            var Q9;
            Q9=makeQuery(id+"F33.opPattern","COPY",BODY,{"derivedFrom":makeQuery(id+"F29.opPattern","COPY",BODY,{"derivedFrom":makeQuery(id+"F8.opPattern","COPY",BODY,{"derivedFrom":makeQuery(id+"F1.opExtrude","SWEPT_BODY",BODY,{"disambiguationData":[OSD([sQuery(id+"F0.wireOp",EDGE,"E0.bottom"),sQuery(id+"F0.wireOp",EDGE,"E0.top"),sQuery(id+"F0.wireOp",EDGE,"E0.left"),sQuery(id+"F0.wireOp",EDGE,"E0.right")])]}),"instanceName":"1"}),"instanceName":"1"}),"instanceName":"1"});
            var Q10;
            Q10=makeQuery(id+"F34.opPattern","COPY",BODY,{"derivedFrom":makeQuery(id+"F33.opPattern","COPY",BODY,{"derivedFrom":makeQuery(id+"F29.opPattern","COPY",BODY,{"derivedFrom":makeQuery(id+"F8.opPattern","COPY",BODY,{"derivedFrom":makeQuery(id+"F1.opExtrude","SWEPT_BODY",BODY,{"disambiguationData":[OSD([sQuery(id+"F0.wireOp",EDGE,"E0.bottom"),sQuery(id+"F0.wireOp",EDGE,"E0.top"),sQuery(id+"F0.wireOp",EDGE,"E0.left"),sQuery(id+"F0.wireOp",EDGE,"E0.right")])]}),"instanceName":"1"}),"instanceName":"1"}),"instanceName":"1"}),"instanceName":"1"});
            transform(context, id + "F40", {"entities" : qUnion([Q0, Q1, Q2, Q3, Q4, Q5, Q6, Q7, Q8, Q9, Q10]), "transformType" : TransformType.TRANSLATION_3D, "dx" : 0 * mm, "dy" : 0 * mm, "dz" : 4 * mm, "makeCopy" : false});
        }
        {
            var Q0;
            Q0=makeQuery(id+"F26.opPattern","COPY",BODY,{"derivedFrom":makeQuery(id+"F23.opPattern","COPY",BODY,{"derivedFrom":makeQuery(id+"F20.opPattern","COPY",BODY,{"derivedFrom":makeQuery(id+"F15.opPattern","COPY",BODY,{"derivedFrom":makeQuery(id+"F13.opPattern","COPY",BODY,{"derivedFrom":makeQuery(id+"F11.opPattern","COPY",BODY,{"derivedFrom":makeQuery(id+"F1.opExtrude","SWEPT_BODY",BODY,{"disambiguationData":[OSD([sQuery(id+"F0.wireOp",EDGE,"E0.bottom"),sQuery(id+"F0.wireOp",EDGE,"E0.top"),sQuery(id+"F0.wireOp",EDGE,"E0.left"),sQuery(id+"F0.wireOp",EDGE,"E0.right")])]}),"instanceName":"1"}),"instanceName":"1"}),"instanceName":"1"}),"instanceName":"1"}),"instanceName":"1"}),"instanceName":"1"});
            transform(context, id + "F41", {"entities" : qUnion([Q0]), "transformType" : TransformType.TRANSLATION_3D, "dx" : 116 * mm, "dy" : 0 * mm, "dz" : 0 * mm, "makeCopy" : true});
        }
        {
            var Q0;
            Q0=makeQuery(id+"F4.opPattern","COPY",BODY,{"derivedFrom":makeQuery(id+"F1.opExtrude","SWEPT_BODY",BODY,{"disambiguationData":[OSD([sQuery(id+"F0.wireOp",EDGE,"E0.bottom"),sQuery(id+"F0.wireOp",EDGE,"E0.top"),sQuery(id+"F0.wireOp",EDGE,"E0.left"),sQuery(id+"F0.wireOp",EDGE,"E0.right")])]}),"instanceName":"1"});
            transform(context, id + "F42", {"entities" : qUnion([Q0]), "transformType" : TransformType.TRANSLATION_3D, "dx" : 0 * mm, "dy" : 0 * mm, "dz" : 117 * mm, "makeCopy" : true});
        }
    });
